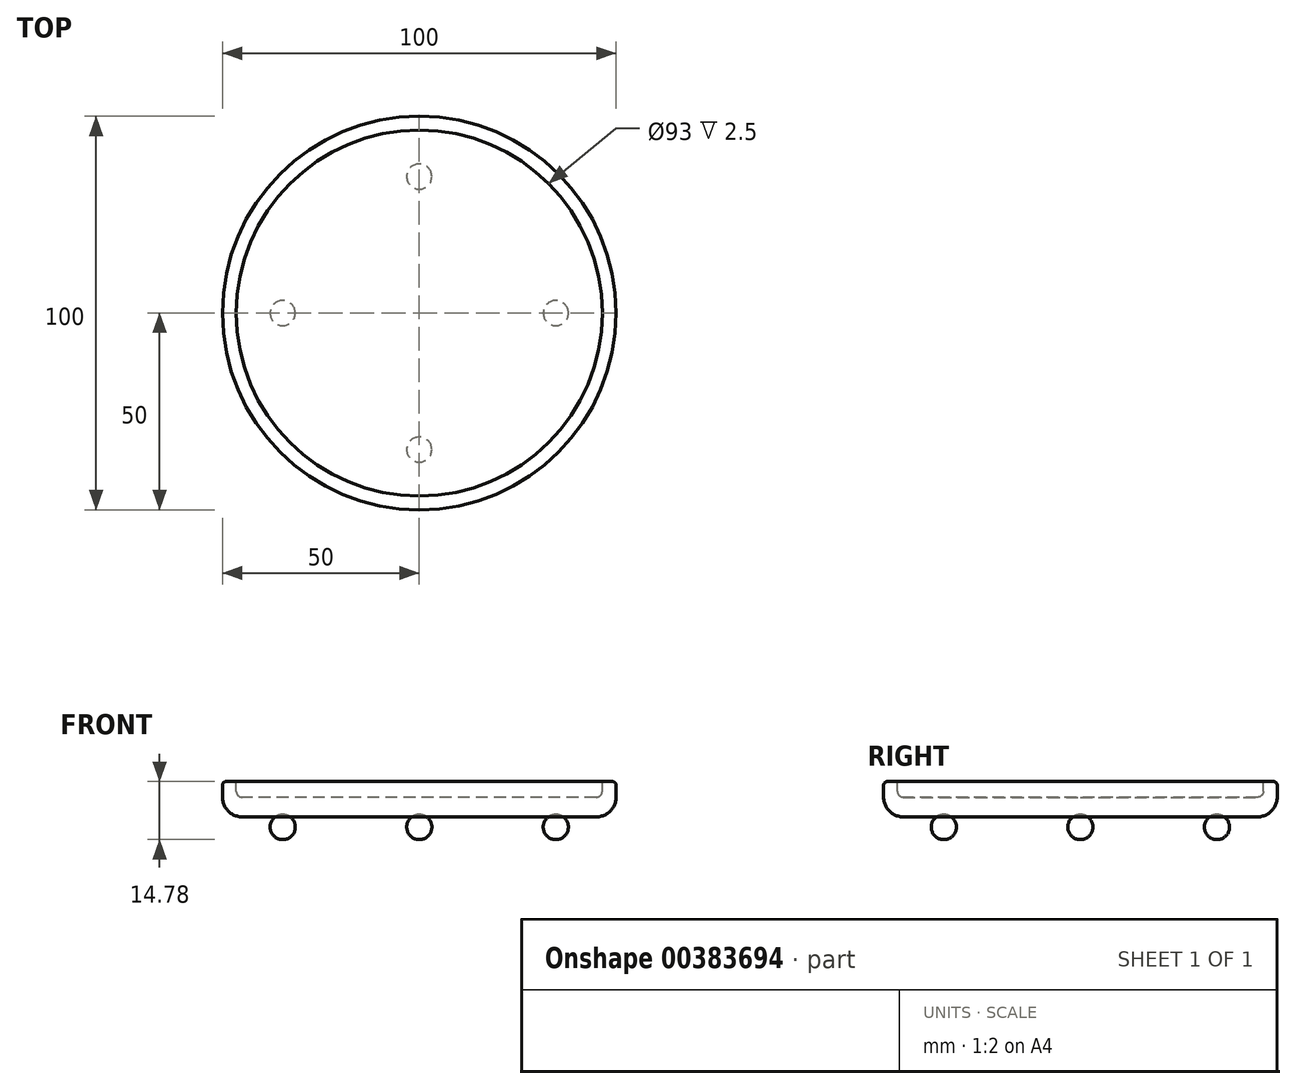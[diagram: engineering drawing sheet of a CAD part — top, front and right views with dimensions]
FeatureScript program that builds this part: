
annotation { "Feature Type Name" : "Feature", "Feature Type Description" : "" }
export const myFeature = defineFeature(function(context is Context, id is Id, definition is map)
    precondition{}
    {
        {
            var Q0;
            Q0=qCreatedBy(makeId("Top.planeOp"),FACE);
            var sketch = newSketch(context, id + "F0", { "sketchPlane" : qUnion([Q0])});
            skCircle(sketch, "E0", {"center": v(0, 0) * mm, "radius": 50 * mm});
            skSolve(sketch);
        }
        {
            var Q0;
            Q0 = qSketchRegion(id + "F0", true);
            extrude(context, id + "F1", {"entities" : qUnion([Q0]), "depth" : 9 * mm});
        }
        {
            var Q0;
            Q0=makeQuery(id+"F1.opExtrude","CAP_FACE",FACE,{"disambiguationData":[OSD([sQuery(id+"F0.wireOp",EDGE,"E0")])],"isStart":false});
            var sketch = newSketch(context, id + "F2", { "sketchPlane" : qUnion([Q0])});
            skCircle(sketch, "E1", {"center": v(0, 0) * mm, "radius": 46.5 * mm});
            skSolve(sketch);
        }
        {
            var Q0;
            Q0=makeQuery(id+"F2.imprint","IMPRINT",FACE,{"disambiguationData":[TD([[makeQuery(id+"F2.imprint","IMPRINT",EDGE,{"derivedFrom":sQuery(id+"F2.wireOp",EDGE,"E1")}),1.0]])]});
            extrude(context, id + "F3", {"entities" : qUnion([Q0]), "operationType" : NewBodyOperationType.REMOVE, "oppositeDirection" : true, "depth" : 4 * mm});
        }
        {
            var Q0;
            Q0=makeQuery(id+"F1.opExtrude","CAP_EDGE",EDGE,{"disambiguationData":[OSD([sQuery(id+"F0.wireOp",EDGE,"E0")])],"isStart":false});
            var Q1;
            Q1=makeQuery(id+"F3.boolean.opBoolean","COPY",EDGE,{"derivedFrom":makeQuery(id+"F3.opExtrude","CAP_EDGE",EDGE,{"disambiguationData":[OSD([sQuery(id+"F2.wireOp",EDGE,"E1")])],"isStart":true})});
            fillet(context, id + "F4", {"entities" : qUnion([Q0, Q1]), "radius" : 1 * mm, "tangentPropagation" : true, "allowEdgeOverflow" : false});
        }
        {
            var Q0;
            Q0=makeQuery(id+"F1.opExtrude","CAP_FACE",FACE,{"disambiguationData":[OSD([sQuery(id+"F0.wireOp",EDGE,"E0")])],"isStart":true});
            fillet(context, id + "F5", {"entities" : qUnion([Q0]), "radius" : 5 * mm, "tangentPropagation" : true, "allowEdgeOverflow" : false});
        }
        {
            var Q0;
            Q0=makeQuery(id+"F3.boolean.opBoolean","COPY",EDGE,{"derivedFrom":makeQuery(id+"F3.opExtrude","CAP_EDGE",EDGE,{"disambiguationData":[OSD([sQuery(id+"F2.wireOp",EDGE,"E1")])],"isStart":false})});
            fillet(context, id + "F6", {"entities" : qUnion([Q0]), "radius" : 1.5 * mm, "tangentPropagation" : true, "allowEdgeOverflow" : false});
        }
        {
            var Q0;
            Q0=makeQuery(id+"F1.opExtrude","CAP_FACE",FACE,{"disambiguationData":[OSD([sQuery(id+"F0.wireOp",EDGE,"E0")])],"isStart":true});
            var sketch = newSketch(context, id + "F7", { "sketchPlane" : qUnion([Q0])});
            skCircle(sketch, "E2", {"center": v(0, 0) * mm, "radius": 35.45 * mm});
            skSolve(sketch);
        }
        {
            var Q0;
            Q0=qCreatedBy(makeId("Front.planeOp"),FACE);
            var sketch = newSketch(context, id + "F8", { "sketchPlane" : qUnion([Q0])});
            skCircle(sketch, "E3", {"center": v(-57.19, 26.52) * mm, "radius": 3.2 * mm});
            skLineSegment(sketch, "E4", {"start": v(-57.19, 34.82) * mm, "end": v(-57.19, 17) * mm});
            skSolve(sketch);
        }
        {
            var Q0;
            {var subQ0=sQuery(id+"F8.wireOp",EDGE,"E4");var subQ1=sQuery(id+"F8.wireOp",EDGE,"E3");var subQ2=makeQuery(id+"F8.imprint","INTERSECT",VERTEX,{"disambiguationData":[OD(0.0)],"derivedFrom":[subQ1,subQ0]});Q0=makeQuery(id+"F8.imprint","IMPRINT",FACE,{"disambiguationData":[TD([[makeQuery(id+"F8.imprint","IMPRINT",EDGE,{"disambiguationData":[TD([[subQ2,1.0]])],"derivedFrom":subQ1}),1.0]])]});}
            var Q1;
            Q1=sQuery(id+"F8.wireOp",EDGE,"E4");
            revolve(context, id + "F9", {"entities" : qUnion([Q0]), "axis" : qUnion([Q1]), "revolveType" : RevolveType.FULL});
        }
        {
            var Q0;
            Q0=makeQuery(id+"F9.opRevolve","SWEPT_BODY",BODY,{"disambiguationData":[OSD([sQuery(id+"F8.wireOp",EDGE,"E3"),sQuery(id+"F8.wireOp",EDGE,"E4")])]});
            transform(context, id + "F10", {"entities" : qUnion([Q0]), "transformType" : TransformType.TRANSLATION_3D, "dx" : 22.5 * mm, "dy" : 0 * mm, "dz" : -29.1 * mm, "makeCopy" : false});
        }
        {
            var Q0;
            Q0=makeQuery(id+"F9.opRevolve","SWEPT_BODY",BODY,{"disambiguationData":[OSD([sQuery(id+"F8.wireOp",EDGE,"E3"),sQuery(id+"F8.wireOp",EDGE,"E4")])]});
            transform(context, id + "F11", {"entities" : qUnion([Q0]), "transformType" : TransformType.COPY});
        }
        {
            var Q0;
            Q0=makeQuery(id+"F9.opRevolve","SWEPT_BODY",BODY,{"disambiguationData":[OSD([sQuery(id+"F8.wireOp",EDGE,"E3"),sQuery(id+"F8.wireOp",EDGE,"E4")])]});
            var Q1;
            Q1=sQuery(id+"F7.wireOp",EDGE,"E2");
            circularPattern(context, id + "F12", {"entities" : qUnion([Q0]), "axis" : qUnion([Q1]), "angle" : 360 * degree, "instanceCount" : 4, "equalSpace" : true});
        }
    });
